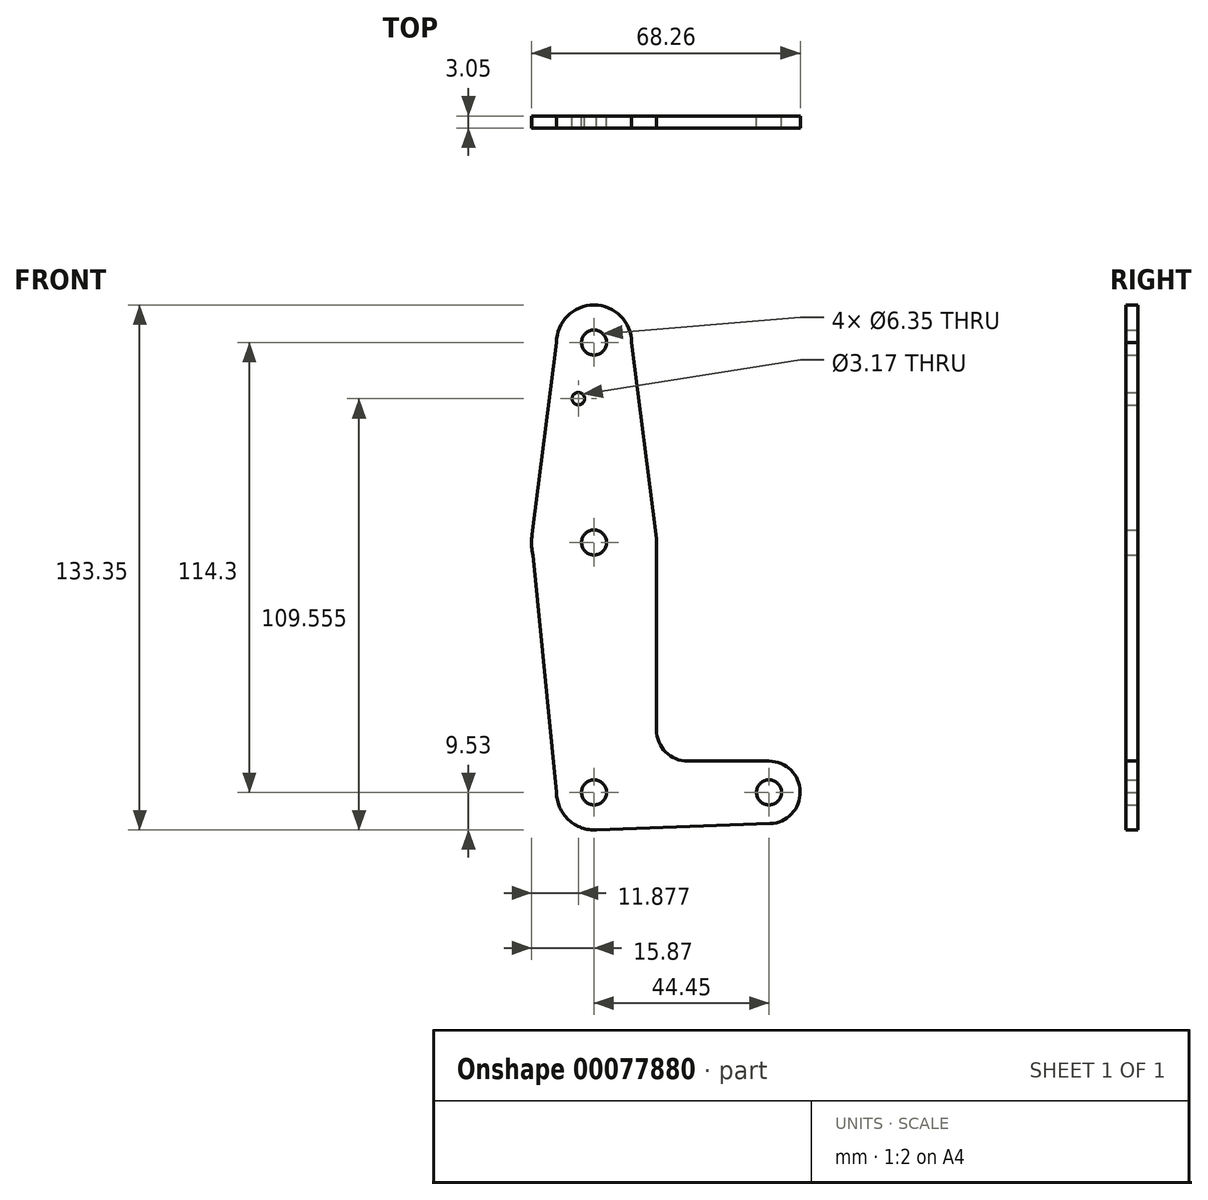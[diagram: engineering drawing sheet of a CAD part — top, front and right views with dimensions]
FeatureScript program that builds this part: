
annotation { "Feature Type Name" : "Feature", "Feature Type Description" : "" }
export const myFeature = defineFeature(function(context is Context, id is Id, definition is map)
    precondition{}
    {
        {
            var Q0;
            Q0=qCreatedBy(makeId("Front.planeOp"),FACE);
            var sketch = newSketch(context, id + "F0", { "sketchPlane" : qUnion([Q0])});
            skCircle(sketch, "E0", {"center": v(0, 0) * mm, "radius": 15.88 * mm});
            skLineSegment(sketch, "E1", {"start": v(0, 50.8) * mm, "end": v(0, 0) * mm, "construction": true});
            skLineSegment(sketch, "E2", {"start": v(0, 0) * mm, "end": v(0, -63.5) * mm, "construction": true});
            skLineSegment(sketch, "E3", {"start": v(0, -63.5) * mm, "end": v(44.45, -63.5) * mm, "construction": true});
            skCircle(sketch, "E4", {"center": v(0, 50.8) * mm, "radius": 9.53 * mm});
            skCircle(sketch, "E5", {"center": v(0, -63.5) * mm, "radius": 9.53 * mm});
            skCircle(sketch, "E6", {"center": v(44.45, -63.5) * mm, "radius": 7.94 * mm});
            skLineSegment(sketch, "E7", {"start": v(-9.52, 50.8) * mm, "end": v(-15.75, 2) * mm});
            skLineSegment(sketch, "E8", {"start": v(15.87, 0) * mm, "end": v(15.88, -47.61) * mm});
            skLineSegment(sketch, "E9", {"start": v(9.53, 50.8) * mm, "end": v(15.88, 1) * mm});
            skLineSegment(sketch, "E10", {"start": v(-15.88, 0) * mm, "end": v(-9.52, -63.5) * mm});
            skLineSegment(sketch, "E11", {"start": v(44.45, -55.56) * mm, "end": v(23.83, -55.56) * mm});
            skCircle(sketch, "E12", {"center": v(0, 50.8) * mm, "radius": 3.18 * mm});
            skCircle(sketch, "E13", {"center": v(0, 0) * mm, "radius": 3.18 * mm});
            skCircle(sketch, "E14", {"center": v(0, -63.5) * mm, "radius": 3.18 * mm});
            skCircle(sketch, "E15", {"center": v(44.45, -63.5) * mm, "radius": 3.18 * mm});
            skArc(sketch, "E16.filletArc", {"start": v(15.88, -47.61) * mm, "mid": v(18.2, -53.23) * mm, "end": v(23.83, -55.56) * mm});
            skLineSegment(sketch, "E17", {"start": v(0, -73.03) * mm, "end": v(44.73, -71.43) * mm});
            skCircle(sketch, "E18", {"center": v(-4, 36.53) * mm, "radius": 1.59 * mm});
            skSolve(sketch);
        }
        {
            var Q0;
            Q0 = qSketchRegion(id + "F0", true);
            extrude(context, id + "F1", {"entities" : qUnion([Q0]), "depth" : 3.05 * mm});
        }
    });
